annotation { "Feature Type Name" : "Feature", "Feature Type Description" : "" }
export const myFeature = defineFeature(function(context is Context, id is Id, definition is map)
    precondition{}
    {
        {
            var Q0;
            Q0=qCreatedBy(makeId("Front.planeOp"),FACE);
            var sketch = newSketch(context, id + "F0", { "sketchPlane" : qUnion([Q0])});
            skLineSegment(sketch, "E0.bottom", {"start": v(-2647.26, 7243.13) * mm, "end": v(2941.24, 7243.13) * mm});
            skLineSegment(sketch, "E0.top", {"start": v(-2647.26, 7086.9) * mm, "end": v(2941.24, 7086.9) * mm});
            skLineSegment(sketch, "E0.left", {"start": v(-2647.26, 7243.13) * mm, "end": v(-2647.26, 7086.9) * mm});
            skLineSegment(sketch, "E0.right", {"start": v(2941.24, 7243.13) * mm, "end": v(2941.24, 7086.9) * mm});
            skLineSegment(sketch, "E1.bottom", {"start": v(-2623.22, 6954.69) * mm, "end": v(-1902.12, 6954.69) * mm});
            skLineSegment(sketch, "E1.top", {"start": v(-2623.22, 6209.56) * mm, "end": v(-1902.12, 6209.56) * mm});
            skLineSegment(sketch, "E1.left", {"start": v(-2623.22, 6954.69) * mm, "end": v(-2623.22, 6209.56) * mm});
            skLineSegment(sketch, "E1.right", {"start": v(-1902.12, 6954.69) * mm, "end": v(-1902.12, 6209.56) * mm});
            skLineSegment(sketch, "E2.bottom", {"start": v(-1601.67, 6966.7) * mm, "end": v(-904.6, 6966.7) * mm});
            skLineSegment(sketch, "E2.top", {"start": v(-1601.67, 6209.56) * mm, "end": v(-904.6, 6209.56) * mm});
            skLineSegment(sketch, "E2.left", {"start": v(-1601.67, 6966.7) * mm, "end": v(-1601.67, 6209.56) * mm});
            skLineSegment(sketch, "E2.right", {"start": v(-904.6, 6966.7) * mm, "end": v(-904.6, 6209.56) * mm});
            skLineSegment(sketch, "E3.bottom", {"start": v(-640.2, 6954.69) * mm, "end": v(20.8, 6954.69) * mm});
            skLineSegment(sketch, "E3.top", {"start": v(-640.2, 6209.56) * mm, "end": v(20.8, 6209.56) * mm});
            skLineSegment(sketch, "E3.left", {"start": v(-640.2, 6954.69) * mm, "end": v(-640.2, 6209.56) * mm});
            skLineSegment(sketch, "E3.right", {"start": v(20.8, 6954.69) * mm, "end": v(20.8, 6209.56) * mm});
            skLineSegment(sketch, "E4.bottom", {"start": v(333.27, 6954.69) * mm, "end": v(958.22, 6954.69) * mm});
            skLineSegment(sketch, "E4.top", {"start": v(333.27, 6221.57) * mm, "end": v(958.22, 6221.57) * mm});
            skLineSegment(sketch, "E4.left", {"start": v(333.27, 6954.69) * mm, "end": v(333.27, 6221.57) * mm});
            skLineSegment(sketch, "E4.right", {"start": v(958.22, 6954.69) * mm, "end": v(958.22, 6221.57) * mm});
            skLineSegment(sketch, "E5.bottom", {"start": v(1258.68, 6966.7) * mm, "end": v(1919.69, 6966.7) * mm});
            skLineSegment(sketch, "E5.top", {"start": v(1258.68, 6233.6) * mm, "end": v(1919.69, 6233.6) * mm});
            skLineSegment(sketch, "E5.left", {"start": v(1258.68, 6966.7) * mm, "end": v(1258.68, 6233.6) * mm});
            skLineSegment(sketch, "E5.right", {"start": v(1919.69, 6966.7) * mm, "end": v(1919.69, 6233.6) * mm});
            skLineSegment(sketch, "E6.bottom", {"start": v(2196.1, 6978.73) * mm, "end": v(2857.11, 6978.73) * mm});
            skLineSegment(sketch, "E6.top", {"start": v(2196.1, 6245.61) * mm, "end": v(2857.11, 6245.61) * mm});
            skLineSegment(sketch, "E6.left", {"start": v(2196.1, 6978.73) * mm, "end": v(2196.1, 6245.61) * mm});
            skLineSegment(sketch, "E6.right", {"start": v(2857.11, 6978.73) * mm, "end": v(2857.11, 6245.61) * mm});
            skLineSegment(sketch, "E7.bottom", {"start": v(-2635.24, 6053.32) * mm, "end": v(2917.2, 6053.32) * mm});
            skLineSegment(sketch, "E7.top", {"start": v(-2635.24, 5885.06) * mm, "end": v(2917.2, 5885.06) * mm});
            skLineSegment(sketch, "E7.left", {"start": v(-2635.24, 6053.32) * mm, "end": v(-2635.24, 5885.06) * mm});
            skLineSegment(sketch, "E7.right", {"start": v(2917.2, 6053.32) * mm, "end": v(2917.2, 5885.06) * mm});
            skLineSegment(sketch, "E8.bottom", {"start": v(-2724.13, -9953.57) * mm, "end": v(2917.2, -9953.57) * mm});
            skLineSegment(sketch, "E8.top", {"start": v(-2724.13, -10145.86) * mm, "end": v(2917.2, -10145.86) * mm});
            skLineSegment(sketch, "E8.left", {"start": v(-2724.13, -9953.57) * mm, "end": v(-2724.13, -10145.86) * mm});
            skLineSegment(sketch, "E8.right", {"start": v(2917.2, -9953.57) * mm, "end": v(2917.2, -10145.86) * mm});
            skLineSegment(sketch, "E9", {"start": v(-2640, -9749.25) * mm, "end": v(-1846.8, -9244.49) * mm});
            skLineSegment(sketch, "E10", {"start": v(-1846.8, -9244.49) * mm, "end": v(-1233.86, -9761.27) * mm});
            skLineSegment(sketch, "E11", {"start": v(-1233.86, -9761.27) * mm, "end": v(-2640, -9749.25) * mm});
            skLineSegment(sketch, "E12", {"start": v(-1450.2, -9208.43) * mm, "end": v(-825.24, -9749.25) * mm});
            skLineSegment(sketch, "E13", {"start": v(-825.24, -9749.25) * mm, "end": v(-212.3, -9184.4) * mm});
            skLineSegment(sketch, "E14", {"start": v(-212.3, -9184.4) * mm, "end": v(-1450.2, -9208.43) * mm});
            skLineSegment(sketch, "E15", {"start": v(154.8, -9208.43) * mm, "end": v(-512.77, -9749.25) * mm});
            skLineSegment(sketch, "E16", {"start": v(-512.77, -9749.25) * mm, "end": v(749.15, -9749.25) * mm});
            skLineSegment(sketch, "E17", {"start": v(749.15, -9749.25) * mm, "end": v(154.8, -9208.43) * mm});
            skLineSegment(sketch, "E18", {"start": v(412.64, -9208.43) * mm, "end": v(1734.65, -9208.43) * mm});
            skLineSegment(sketch, "E19", {"start": v(1734.65, -9208.43) * mm, "end": v(1097.68, -9749.25) * mm});
            skLineSegment(sketch, "E20", {"start": v(1097.68, -9749.25) * mm, "end": v(412.64, -9208.43) * mm});
            skLineSegment(sketch, "E21", {"start": v(1410.16, -9749.25) * mm, "end": v(2059.14, -9208.43) * mm});
            skLineSegment(sketch, "E22", {"start": v(2059.14, -9208.43) * mm, "end": v(2804.28, -9749.25) * mm});
            skLineSegment(sketch, "E23", {"start": v(2804.28, -9749.25) * mm, "end": v(1410.16, -9749.25) * mm});
            skLineSegment(sketch, "E24", {"start": v(-2711.48, -9070.63) * mm, "end": v(2939.83, -9070.63) * mm});
            skLineSegment(sketch, "E25", {"start": v(2939.83, -9070.63) * mm, "end": v(2948.32, -8892.16) * mm});
            skLineSegment(sketch, "E26", {"start": v(2948.32, -8892.16) * mm, "end": v(-2728.47, -8892.16) * mm});
            skLineSegment(sketch, "E27", {"start": v(-2728.47, -8892.16) * mm, "end": v(-2711.48, -9070.63) * mm});
            skLineSegment(sketch, "E28", {"start": v(-1807.58, 3153.54) * mm, "end": v(-924.79, 3394.3) * mm});
            skLineSegment(sketch, "E29", {"start": v(-416.63, 3043.15) * mm, "end": v(-1807.58, 3153.54) * mm});
            skLineSegment(sketch, "E30", {"start": v(-924.79, 3394.3) * mm, "end": v(-416.63, 3043.15) * mm});
            skLineSegment(sketch, "E31", {"start": v(-1785.5, 2976.91) * mm, "end": v(1526.28, 2822.36) * mm});
            skLineSegment(sketch, "E32", {"start": v(1526.28, 2822.36) * mm, "end": v(1879.54, 2071.69) * mm});
            skLineSegment(sketch, "E33", {"start": v(1879.54, 2071.69) * mm, "end": v(-1785.5, 2976.91) * mm});
            skLineSegment(sketch, "E34", {"start": v(-1807.58, 2976.91) * mm, "end": v(-2624.5, 2248.32) * mm});
            skLineSegment(sketch, "E35", {"start": v(-2624.5, 2248.32) * mm, "end": v(2122.4, 1740.51) * mm});
            skLineSegment(sketch, "E36", {"start": v(2122.4, 1740.51) * mm, "end": v(-1807.58, 2976.91) * mm});
            skLineSegment(sketch, "E37", {"start": v(-2338.94, 1958.15) * mm, "end": v(2739.14, 1538.65) * mm});
            skLineSegment(sketch, "E38", {"start": v(2739.14, 1538.65) * mm, "end": v(1748.92, -27.27) * mm});
            skLineSegment(sketch, "E39", {"start": v(1748.92, -27.27) * mm, "end": v(-2338.94, 1958.15) * mm});
            skLineSegment(sketch, "E40", {"start": v(-2514.1, 1860.85) * mm, "end": v(-2514.1, 746.97) * mm});
            skLineSegment(sketch, "E41", {"start": v(-2514.1, 746.97) * mm, "end": v(-261.08, 746.97) * mm});
            skLineSegment(sketch, "E42", {"start": v(-261.08, 746.97) * mm, "end": v(-2514.1, 1860.85) * mm});
            skLineSegment(sketch, "E43", {"start": v(154.8, 746.97) * mm, "end": v(1529.38, -351.7) * mm});
            skLineSegment(sketch, "E44", {"start": v(1529.38, -351.7) * mm, "end": v(-1343.93, 570.35) * mm});
            skLineSegment(sketch, "E45", {"start": v(-1343.93, 570.35) * mm, "end": v(154.8, 746.97) * mm});
            skLineSegment(sketch, "E46", {"start": v(-1785.5, 570.35) * mm, "end": v(1415.9, -379.03) * mm});
            skLineSegment(sketch, "E47", {"start": v(1415.9, -379.03) * mm, "end": v(-1189.38, -908.92) * mm});
            skLineSegment(sketch, "E48", {"start": v(-1189.38, -908.92) * mm, "end": v(-1785.5, 570.35) * mm});
            skLineSegment(sketch, "E49", {"start": v(-924.79, -1011.13) * mm, "end": v(1555.15, -469.79) * mm});
            skLineSegment(sketch, "E50", {"start": v(1555.15, -469.79) * mm, "end": v(1760.27, -1409.45) * mm});
            skLineSegment(sketch, "E51", {"start": v(1760.27, -1409.45) * mm, "end": v(-924.79, -1011.13) * mm});
            skLineSegment(sketch, "E52", {"start": v(-1061.16, -1124.6) * mm, "end": v(-1215.71, -1551.64) * mm});
            skLineSegment(sketch, "E53", {"start": v(-1215.71, -1551.64) * mm, "end": v(1680.83, -1637.51) * mm});
            skLineSegment(sketch, "E54", {"start": v(1680.83, -1637.51) * mm, "end": v(-1061.16, -1124.6) * mm});
            skLineSegment(sketch, "E55", {"start": v(-1061.16, -1750.34) * mm, "end": v(1482.13, -1924.54) * mm});
            skLineSegment(sketch, "E56", {"start": v(1482.13, -1924.54) * mm, "end": v(400.28, -3536.27) * mm});
            skLineSegment(sketch, "E57", {"start": v(400.28, -3536.27) * mm, "end": v(-1061.16, -1750.34) * mm});
            skLineSegment(sketch, "E58", {"start": v(-1017, -2048.4) * mm, "end": v(-129.61, -3425.88) * mm});
            skLineSegment(sketch, "E59", {"start": v(-129.61, -3425.88) * mm, "end": v(-703.65, -3757.06) * mm});
            skLineSegment(sketch, "E60", {"start": v(-703.65, -3757.06) * mm, "end": v(-1017, -2048.4) * mm});
            skSolve(sketch);
        }
        {
            var Q0;
            Q0=makeQuery(id+"F0.imprint","IMPRINT",FACE,{"disambiguationData":[TD([[makeQuery(id+"F0.imprint","IMPRINT",EDGE,{"derivedFrom":sQuery(id+"F0.wireOp",EDGE,"E40")}),1.0]])]});
            var Q1;
            Q1=makeQuery(id+"F0.imprint","IMPRINT",FACE,{"disambiguationData":[TD([[makeQuery(id+"F0.imprint","IMPRINT",EDGE,{"derivedFrom":sQuery(id+"F0.wireOp",EDGE,"E46")}),-1.0]])]});
            var Q2;
            Q2=makeQuery(id+"F0.imprint","IMPRINT",FACE,{"disambiguationData":[TD([[makeQuery(id+"F0.imprint","IMPRINT",EDGE,{"derivedFrom":sQuery(id+"F0.wireOp",EDGE,"E49")}),-1.0]])]});
            var Q3;
            Q3=makeQuery(id+"F0.imprint","IMPRINT",FACE,{"disambiguationData":[TD([[makeQuery(id+"F0.imprint","IMPRINT",EDGE,{"derivedFrom":sQuery(id+"F0.wireOp",EDGE,"E21")}),-1.0]])]});
            var Q4;
            Q4=makeQuery(id+"F0.imprint","IMPRINT",FACE,{"disambiguationData":[TD([[makeQuery(id+"F0.imprint","IMPRINT",EDGE,{"derivedFrom":sQuery(id+"F0.wireOp",EDGE,"E31")}),-1.0]])]});
            var Q5;
            Q5=makeQuery(id+"F0.imprint","IMPRINT",FACE,{"disambiguationData":[TD([[makeQuery(id+"F0.imprint","IMPRINT",EDGE,{"derivedFrom":sQuery(id+"F0.wireOp",EDGE,"E1.bottom")}),-1.0]])]});
            var Q6;
            Q6=makeQuery(id+"F0.imprint","IMPRINT",FACE,{"disambiguationData":[TD([[makeQuery(id+"F0.imprint","IMPRINT",EDGE,{"derivedFrom":sQuery(id+"F0.wireOp",EDGE,"E2.bottom")}),-1.0]])]});
            var Q7;
            Q7=makeQuery(id+"F0.imprint","IMPRINT",FACE,{"disambiguationData":[TD([[makeQuery(id+"F0.imprint","IMPRINT",EDGE,{"derivedFrom":sQuery(id+"F0.wireOp",EDGE,"E3.bottom")}),-1.0]])]});
            var Q8;
            Q8=makeQuery(id+"F0.imprint","IMPRINT",FACE,{"disambiguationData":[TD([[makeQuery(id+"F0.imprint","IMPRINT",EDGE,{"derivedFrom":sQuery(id+"F0.wireOp",EDGE,"E4.bottom")}),-1.0]])]});
            var Q9;
            Q9=makeQuery(id+"F0.imprint","IMPRINT",FACE,{"disambiguationData":[TD([[makeQuery(id+"F0.imprint","IMPRINT",EDGE,{"derivedFrom":sQuery(id+"F0.wireOp",EDGE,"E5.bottom")}),-1.0]])]});
            var Q10;
            Q10=makeQuery(id+"F0.imprint","IMPRINT",FACE,{"disambiguationData":[TD([[makeQuery(id+"F0.imprint","IMPRINT",EDGE,{"derivedFrom":sQuery(id+"F0.wireOp",EDGE,"E6.bottom")}),-1.0]])]});
            var Q11;
            Q11=makeQuery(id+"F0.imprint","IMPRINT",FACE,{"disambiguationData":[TD([[makeQuery(id+"F0.imprint","IMPRINT",EDGE,{"derivedFrom":sQuery(id+"F0.wireOp",EDGE,"E8.bottom")}),-1.0]])]});
            var Q12;
            Q12=makeQuery(id+"F0.imprint","IMPRINT",FACE,{"disambiguationData":[TD([[makeQuery(id+"F0.imprint","IMPRINT",EDGE,{"derivedFrom":sQuery(id+"F0.wireOp",EDGE,"E9")}),-1.0]])]});
            var Q13;
            Q13=makeQuery(id+"F0.imprint","IMPRINT",FACE,{"disambiguationData":[TD([[makeQuery(id+"F0.imprint","IMPRINT",EDGE,{"derivedFrom":sQuery(id+"F0.wireOp",EDGE,"E12")}),1.0]])]});
            var Q14;
            Q14=makeQuery(id+"F0.imprint","IMPRINT",FACE,{"disambiguationData":[TD([[makeQuery(id+"F0.imprint","IMPRINT",EDGE,{"derivedFrom":sQuery(id+"F0.wireOp",EDGE,"E15")}),1.0]])]});
            var Q15;
            Q15=makeQuery(id+"F0.imprint","IMPRINT",FACE,{"disambiguationData":[TD([[makeQuery(id+"F0.imprint","IMPRINT",EDGE,{"derivedFrom":sQuery(id+"F0.wireOp",EDGE,"E18")}),-1.0]])]});
            var Q16;
            Q16=makeQuery(id+"F0.imprint","IMPRINT",FACE,{"disambiguationData":[TD([[makeQuery(id+"F0.imprint","IMPRINT",EDGE,{"derivedFrom":sQuery(id+"F0.wireOp",EDGE,"E52")}),1.0]])]});
            var Q17;
            Q17=makeQuery(id+"F0.imprint","IMPRINT",FACE,{"disambiguationData":[TD([[makeQuery(id+"F0.imprint","IMPRINT",EDGE,{"derivedFrom":sQuery(id+"F0.wireOp",EDGE,"E34")}),1.0]])]});
            var Q18;
            Q18=makeQuery(id+"F0.imprint","IMPRINT",FACE,{"disambiguationData":[TD([[makeQuery(id+"F0.imprint","IMPRINT",EDGE,{"derivedFrom":sQuery(id+"F0.wireOp",EDGE,"E55")}),-1.0]])]});
            var Q19;
            {var subQ0=sQuery(id+"F0.wireOp",EDGE,"E37");Q19=makeQuery(id+"F0.imprint","IMPRINT",FACE,{"disambiguationData":[TD([[makeQuery(id+"F0.imprint","IMPRINT",EDGE,{"derivedFrom":subQ0}),-1.0]])]});}
            var Q20;
            Q20=makeQuery(id+"F0.imprint","IMPRINT",FACE,{"disambiguationData":[TD([[makeQuery(id+"F0.imprint","IMPRINT",EDGE,{"derivedFrom":sQuery(id+"F0.wireOp",EDGE,"E58")}),-1.0]])]});
            var Q21;
            Q21=makeQuery(id+"F0.imprint","IMPRINT",FACE,{"disambiguationData":[TD([[makeQuery(id+"F0.imprint","IMPRINT",EDGE,{"derivedFrom":sQuery(id+"F0.wireOp",EDGE,"E43")}),-1.0]])]});
            var Q22;
            Q22=makeQuery(id+"F0.imprint","IMPRINT",FACE,{"disambiguationData":[TD([[makeQuery(id+"F0.imprint","IMPRINT",EDGE,{"derivedFrom":sQuery(id+"F0.wireOp",EDGE,"E28")}),-1.0]])]});
            var Q23;
            Q23=makeQuery(id+"F0.imprint","IMPRINT",FACE,{"disambiguationData":[TD([[makeQuery(id+"F0.imprint","IMPRINT",EDGE,{"derivedFrom":sQuery(id+"F0.wireOp",EDGE,"E24")}),1.0]])]});
            var Q24;
            Q24=makeQuery(id+"F0.imprint","IMPRINT",FACE,{"disambiguationData":[TD([[makeQuery(id+"F0.imprint","IMPRINT",EDGE,{"derivedFrom":sQuery(id+"F0.wireOp",EDGE,"E0.bottom")}),-1.0]])]});
            var Q25;
            Q25=makeQuery(id+"F0.imprint","IMPRINT",FACE,{"disambiguationData":[TD([[makeQuery(id+"F0.imprint","IMPRINT",EDGE,{"derivedFrom":sQuery(id+"F0.wireOp",EDGE,"E7.bottom")}),-1.0]])]});
            extrude(context, id + "F1", {"entities" : qUnion([Q0, Q1, Q2, Q3, Q4, Q5, Q6, Q7, Q8, Q9, Q10, Q11, Q12, Q13, Q14, Q15, Q16, Q17, Q18, Q19, Q20, Q21, Q22, Q23, Q24, Q25]), "depth" : 25 * mm, "offsetDistance" : 25 * mm});
        }
    });